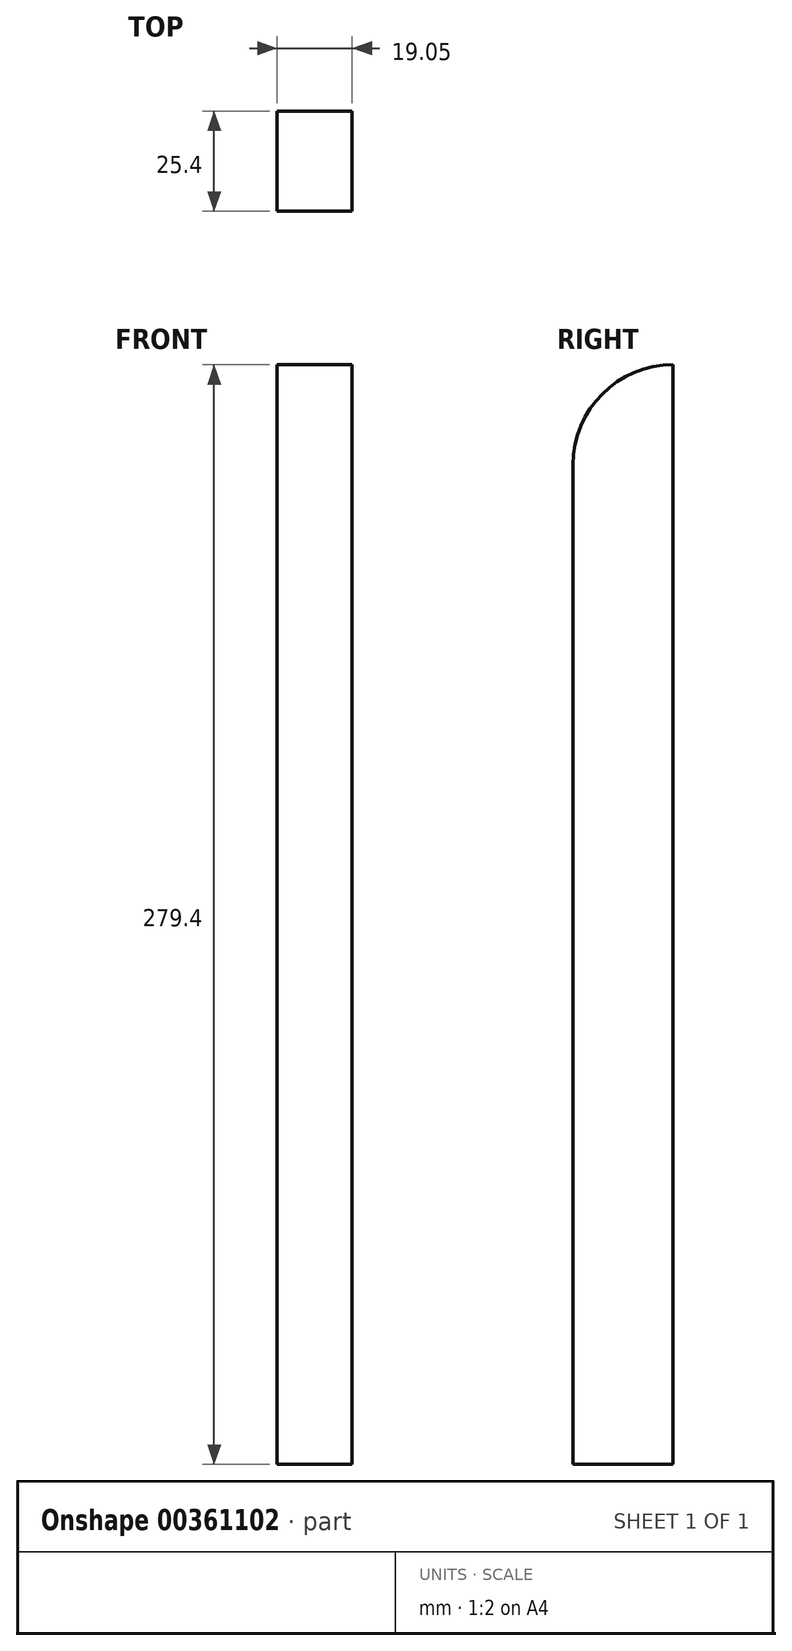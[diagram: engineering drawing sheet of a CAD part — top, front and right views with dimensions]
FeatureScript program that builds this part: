
annotation { "Feature Type Name" : "Feature", "Feature Type Description" : "" }
export const myFeature = defineFeature(function(context is Context, id is Id, definition is map)
    precondition{}
    {
        {
            var Q0;
            Q0=qCreatedBy(makeId("Right.planeOp"),FACE);
            var sketch = newSketch(context, id + "F0", { "sketchPlane" : qUnion([Q0])});
            skLineSegment(sketch, "E0.top", {"start": v(-106.3, -104.24) * mm, "end": v(-80.9, -104.24) * mm});
            skLineSegment(sketch, "E0.left", {"start": v(-106.3, 137.06) * mm, "end": v(-106.3, -104.24) * mm});
            skLineSegment(sketch, "E0.right", {"start": v(-80.9, 175.16) * mm, "end": v(-80.9, -104.24) * mm});
            skPoint(sketch, "E1.orphan", {"position": v(-106.3, 160.27) * mm});
            skLineSegment(sketch, "E2", {"start": v(-106.3, 149.76) * mm, "end": v(-106.3, 137.06) * mm});
            skLineSegment(sketch, "E3", {"start": v(-80.9, 175.16) * mm, "end": v(-80.9, 175.16) * mm});
            skPoint(sketch, "E4.visualSharp", {"position": v(-106.3, 175.16) * mm});
            skArc(sketch, "E4.filletArc", {"start": v(-80.9, 175.16) * mm, "mid": v(-98.85, 167.72) * mm, "end": v(-106.3, 149.76) * mm});
            skSolve(sketch);
        }
        {
            var Q0;
            Q0=qSketchRegion(id+"F0",true);
            extrude(context, id + "F1", {"entities" : qUnion([Q0]), "depth" : 19.05 * mm});
        }
    });
